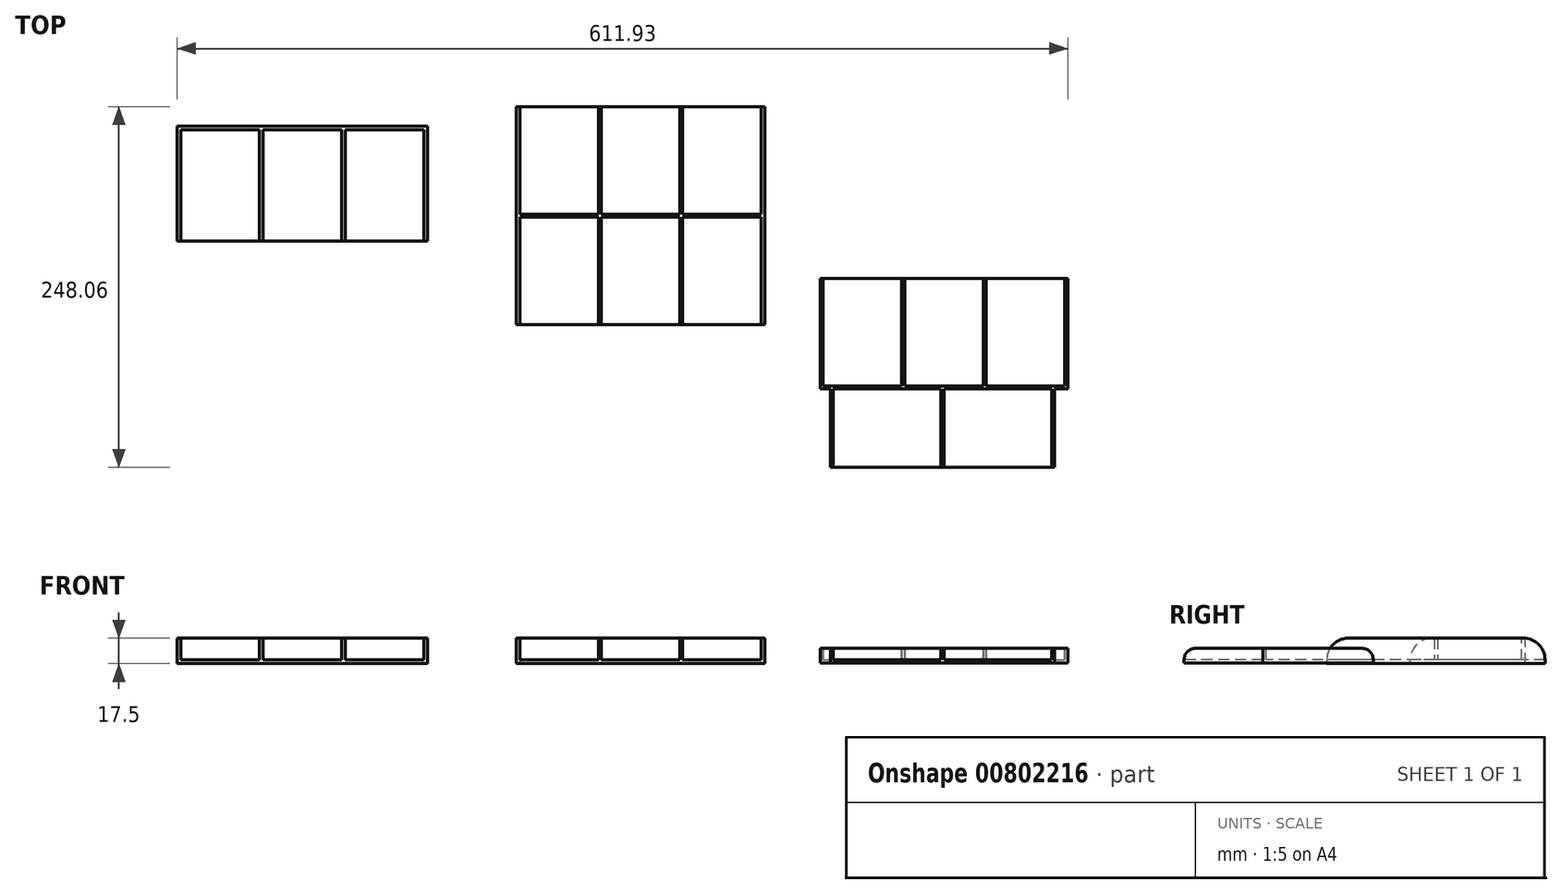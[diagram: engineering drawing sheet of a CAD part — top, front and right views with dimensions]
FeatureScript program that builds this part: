
annotation { "Feature Type Name" : "Feature", "Feature Type Description" : "" }
export const myFeature = defineFeature(function(context is Context, id is Id, definition is map)
    precondition{}
    {
        {
            var Q0;
            Q0=qCreatedBy(makeId("Top.planeOp"),FACE);
            var sketch = newSketch(context, id + "F0", { "sketchPlane" : qUnion([Q0])});
            skLineSegment(sketch, "E0.bottom", {"start": v(-93.78, 44.89) * mm, "end": v(-39.78, 44.89) * mm});
            skLineSegment(sketch, "E0.top", {"start": v(-93.78, -29.11) * mm, "end": v(-39.78, -29.11) * mm});
            skLineSegment(sketch, "E0.left", {"start": v(-93.78, 44.89) * mm, "end": v(-93.78, -29.11) * mm});
            skLineSegment(sketch, "E0.right", {"start": v(-39.78, 44.89) * mm, "end": v(-39.78, -29.11) * mm});
            skLineSegment(sketch, "E1.1.0.0", {"start": v(16.72, 44.89) * mm, "end": v(16.72, -29.11) * mm});
            skLineSegment(sketch, "E1.1.0.1", {"start": v(-37.28, -29.11) * mm, "end": v(16.72, -29.11) * mm});
            skLineSegment(sketch, "E1.1.0.2", {"start": v(-37.28, 44.89) * mm, "end": v(-37.28, -29.11) * mm});
            skLineSegment(sketch, "E1.1.0.3", {"start": v(-37.28, 44.89) * mm, "end": v(16.72, 44.89) * mm});
            skLineSegment(sketch, "E1.2.0.0", {"start": v(73.22, 44.89) * mm, "end": v(73.22, -29.11) * mm});
            skLineSegment(sketch, "E1.2.0.1", {"start": v(19.22, -29.11) * mm, "end": v(73.22, -29.11) * mm});
            skLineSegment(sketch, "E1.2.0.2", {"start": v(19.22, 44.89) * mm, "end": v(19.22, -29.11) * mm});
            skLineSegment(sketch, "E1.2.0.3", {"start": v(19.22, 44.89) * mm, "end": v(73.22, 44.89) * mm});
            skLineSegment(sketch, "E1.direction1", {"start": v(-39.78, -29.11) * mm, "end": v(16.72, -29.11) * mm, "construction": true});
            skLineSegment(sketch, "E2", {"start": v(-96.28, 47.39) * mm, "end": v(-96.28, -31.61) * mm});
            skLineSegment(sketch, "E3", {"start": v(-96.28, -31.61) * mm, "end": v(75.72, -31.61) * mm});
            skLineSegment(sketch, "E4", {"start": v(75.72, -31.61) * mm, "end": v(75.72, 47.39) * mm});
            skLineSegment(sketch, "E5", {"start": v(75.72, 47.39) * mm, "end": v(-96.28, 47.39) * mm});
            skSolve(sketch);
        }
        {
            var Q0;
            Q0=makeQuery(id+"F0.imprint","IMPRINT",FACE,{"disambiguationData":[TD([[makeQuery(id+"F0.imprint","IMPRINT",EDGE,{"derivedFrom":sQuery(id+"F0.wireOp",EDGE,"E0.bottom")}),1.0]])]});
            extrude(context, id + "F1", {"entities" : qUnion([Q0]), "depth" : 15 * mm, "offsetDistance" : 25 * mm});
        }
        {
            var Q0;
            Q0=makeQuery(id+"F1.opExtrude","CAP_FACE",FACE,{"disambiguationData":[OSD([sQuery(id+"F0.wireOp",EDGE,"E0.bottom"),sQuery(id+"F0.wireOp",EDGE,"E0.top"),sQuery(id+"F0.wireOp",EDGE,"E0.left"),sQuery(id+"F0.wireOp",EDGE,"E0.right"),sQuery(id+"F0.wireOp",EDGE,"E1.1.0.0"),sQuery(id+"F0.wireOp",EDGE,"E1.1.0.1"),sQuery(id+"F0.wireOp",EDGE,"E1.1.0.2"),sQuery(id+"F0.wireOp",EDGE,"E1.1.0.3"),sQuery(id+"F0.wireOp",EDGE,"E1.2.0.0"),sQuery(id+"F0.wireOp",EDGE,"E1.2.0.1"),sQuery(id+"F0.wireOp",EDGE,"E1.2.0.2"),sQuery(id+"F0.wireOp",EDGE,"E1.2.0.3"),sQuery(id+"F0.wireOp",EDGE,"E1.3.0.0"),sQuery(id+"F0.wireOp",EDGE,"E1.3.0.1"),sQuery(id+"F0.wireOp",EDGE,"E1.3.0.2"),sQuery(id+"F0.wireOp",EDGE,"E1.3.0.3"),sQuery(id+"F0.wireOp",EDGE,"E1.4.0.0"),sQuery(id+"F0.wireOp",EDGE,"E1.4.0.1"),sQuery(id+"F0.wireOp",EDGE,"E1.4.0.2"),sQuery(id+"F0.wireOp",EDGE,"E1.4.0.3"),sQuery(id+"F0.wireOp",EDGE,"E1.5.0.0"),sQuery(id+"F0.wireOp",EDGE,"E1.5.0.1"),sQuery(id+"F0.wireOp",EDGE,"E1.5.0.2"),sQuery(id+"F0.wireOp",EDGE,"E1.5.0.3"),sQuery(id+"F0.wireOp",EDGE,"E1.6.0.0"),sQuery(id+"F0.wireOp",EDGE,"E1.6.0.1"),sQuery(id+"F0.wireOp",EDGE,"E1.6.0.2"),sQuery(id+"F0.wireOp",EDGE,"E1.6.0.3"),sQuery(id+"F0.wireOp",EDGE,"E1.7.0.0"),sQuery(id+"F0.wireOp",EDGE,"E1.7.0.1"),sQuery(id+"F0.wireOp",EDGE,"E1.7.0.2"),sQuery(id+"F0.wireOp",EDGE,"E1.7.0.3"),sQuery(id+"F0.wireOp",EDGE,"E2"),sQuery(id+"F0.wireOp",EDGE,"E3"),sQuery(id+"F0.wireOp",EDGE,"E4"),sQuery(id+"F0.wireOp",EDGE,"E5")])],"isStart":false});
            var sketch = newSketch(context, id + "F2", { "sketchPlane" : qUnion([Q0])});
            skSolve(sketch);
        }
        {
            var Q0;
            Q0=makeQuery(id+"F2.imprint","IMPRINT",FACE,{"disambiguationData":[TD([[makeQuery(id+"F2.imprint","IMPRINT",EDGE,{"derivedFrom":makeQuery(id+"F1.opExtrude","CAP_EDGE",EDGE,{"disambiguationData":[OSD([sQuery(id+"F0.wireOp",EDGE,"E0.bottom")])],"isStart":false})}),1.0]])]});
            var Q1;
            Q1=makeQuery(id+"F2.imprint","IMPRINT",FACE,{"disambiguationData":[TD([[makeQuery(id+"F2.imprint","IMPRINT",EDGE,{"derivedFrom":makeQuery(id+"F1.opExtrude","CAP_EDGE",EDGE,{"disambiguationData":[OSD([sQuery(id+"F0.wireOp",EDGE,"E0.bottom")])],"isStart":false})}),-1.0]])]});
            var Q2;
            Q2=makeQuery(id+"F2.imprint","IMPRINT",FACE,{"disambiguationData":[TD([[makeQuery(id+"F2.imprint","IMPRINT",EDGE,{"derivedFrom":makeQuery(id+"F1.opExtrude","CAP_EDGE",EDGE,{"disambiguationData":[OSD([sQuery(id+"F0.wireOp",EDGE,"E1.1.0.0")])],"isStart":false})}),-1.0]])]});
            var Q3;
            Q3=makeQuery(id+"F2.imprint","IMPRINT",FACE,{"disambiguationData":[TD([[makeQuery(id+"F2.imprint","IMPRINT",EDGE,{"derivedFrom":makeQuery(id+"F1.opExtrude","CAP_EDGE",EDGE,{"disambiguationData":[OSD([sQuery(id+"F0.wireOp",EDGE,"E1.2.0.0")])],"isStart":false})}),-1.0]])]});
            var Q4;
            Q4=makeQuery(id+"F2.imprint","IMPRINT",FACE,{"disambiguationData":[TD([[makeQuery(id+"F2.imprint","IMPRINT",EDGE,{"derivedFrom":makeQuery(id+"F1.opExtrude","CAP_EDGE",EDGE,{"disambiguationData":[OSD([sQuery(id+"F0.wireOp",EDGE,"E1.3.0.0")])],"isStart":false})}),-1.0]])]});
            var Q5;
            Q5=makeQuery(id+"F2.imprint","IMPRINT",FACE,{"disambiguationData":[TD([[makeQuery(id+"F2.imprint","IMPRINT",EDGE,{"derivedFrom":makeQuery(id+"F1.opExtrude","CAP_EDGE",EDGE,{"disambiguationData":[OSD([sQuery(id+"F0.wireOp",EDGE,"E1.4.0.0")])],"isStart":false})}),-1.0]])]});
            var Q6;
            Q6=makeQuery(id+"F2.imprint","IMPRINT",FACE,{"disambiguationData":[TD([[makeQuery(id+"F2.imprint","IMPRINT",EDGE,{"derivedFrom":makeQuery(id+"F1.opExtrude","CAP_EDGE",EDGE,{"disambiguationData":[OSD([sQuery(id+"F0.wireOp",EDGE,"E1.5.0.0")])],"isStart":false})}),-1.0]])]});
            var Q7;
            Q7=makeQuery(id+"F2.imprint","IMPRINT",FACE,{"disambiguationData":[TD([[makeQuery(id+"F2.imprint","IMPRINT",EDGE,{"derivedFrom":makeQuery(id+"F1.opExtrude","CAP_EDGE",EDGE,{"disambiguationData":[OSD([sQuery(id+"F0.wireOp",EDGE,"E1.6.0.0")])],"isStart":false})}),-1.0]])]});
            var Q8;
            Q8=makeQuery(id+"F2.imprint","IMPRINT",FACE,{"disambiguationData":[TD([[makeQuery(id+"F2.imprint","IMPRINT",EDGE,{"derivedFrom":makeQuery(id+"F1.opExtrude","CAP_EDGE",EDGE,{"disambiguationData":[OSD([sQuery(id+"F0.wireOp",EDGE,"E1.7.0.0")])],"isStart":false})}),-1.0]])]});
            extrude(context, id + "F3", {"entities" : qUnion([Q0, Q1, Q2, Q3, Q4, Q5, Q6, Q7, Q8]), "operationType" : NewBodyOperationType.ADD, "depth" : 2.5 * mm, "offsetDistance" : 25 * mm});
        }
        {
            var Q0;
            Q0=makeQuery(id+"F1.opExtrude","SWEPT_FACE",FACE,{"disambiguationData":[OSD([sQuery(id+"F0.wireOp",EDGE,"E0.top")])]});
            var Q1;
            Q1=makeQuery(id+"F1.opExtrude","SWEPT_FACE",FACE,{"disambiguationData":[OSD([sQuery(id+"F0.wireOp",EDGE,"E1.1.0.1")])]});
            var Q2;
            Q2=makeQuery(id+"F1.opExtrude","SWEPT_FACE",FACE,{"disambiguationData":[OSD([sQuery(id+"F0.wireOp",EDGE,"E1.2.0.1")])]});
            var Q3;
            Q3=makeQuery(id+"F1.opExtrude","SWEPT_FACE",FACE,{"disambiguationData":[OSD([sQuery(id+"F0.wireOp",EDGE,"E1.3.0.1")])]});
            var Q4;
            Q4=makeQuery(id+"F1.opExtrude","SWEPT_FACE",FACE,{"disambiguationData":[OSD([sQuery(id+"F0.wireOp",EDGE,"E1.4.0.1")])]});
            var Q5;
            Q5=makeQuery(id+"F1.opExtrude","SWEPT_FACE",FACE,{"disambiguationData":[OSD([sQuery(id+"F0.wireOp",EDGE,"E1.5.0.1")])]});
            var Q6;
            Q6=makeQuery(id+"F1.opExtrude","SWEPT_FACE",FACE,{"disambiguationData":[OSD([sQuery(id+"F0.wireOp",EDGE,"E1.6.0.1")])]});
            var Q7;
            Q7=makeQuery(id+"F1.opExtrude","SWEPT_FACE",FACE,{"disambiguationData":[OSD([sQuery(id+"F0.wireOp",EDGE,"E1.7.0.1")])]});
            extrude(context, id + "F4", {"entities" : qUnion([Q0, Q1, Q2, Q3, Q4, Q5, Q6, Q7]), "operationType" : NewBodyOperationType.REMOVE, "oppositeDirection" : true, "depth" : 5 * mm, "offsetDistance" : 25 * mm});
        }
        {
            var Q0;
            {var subQ0=sQuery(id+"F0.wireOp",EDGE,"E3");var subQ1=sQuery(id+"F0.wireOp",EDGE,"E1.7.0.0");Q0=makeQuery(id+"F4.boolean.opBoolean","SPLIT",EDGE,{"disambiguationData":[TD([makeQuery(id+"F1.opExtrude","SWEPT_FACE",FACE,{"disambiguationData":[OSD([subQ1])]})])],"derivedFrom":makeQuery(id+"F1.opExtrude","CAP_EDGE",EDGE,{"disambiguationData":[OSD([subQ0])],"isStart":true})});}
            var Q1;
            {var subQ0=sQuery(id+"F0.wireOp",EDGE,"E3");var subQ4=sQuery(id+"F0.wireOp",EDGE,"E1.6.0.0");Q1=makeQuery(id+"F4.boolean.opBoolean","SPLIT",EDGE,{"disambiguationData":[TD([makeQuery(id+"F1.opExtrude","SWEPT_FACE",FACE,{"disambiguationData":[OSD([subQ4])]})])],"derivedFrom":makeQuery(id+"F1.opExtrude","CAP_EDGE",EDGE,{"disambiguationData":[OSD([subQ0])],"isStart":true})});}
            var Q2;
            {var subQ0=sQuery(id+"F0.wireOp",EDGE,"E3");var subQ2=sQuery(id+"F0.wireOp",EDGE,"E1.5.0.0");Q2=makeQuery(id+"F4.boolean.opBoolean","SPLIT",EDGE,{"disambiguationData":[TD([makeQuery(id+"F1.opExtrude","SWEPT_FACE",FACE,{"disambiguationData":[OSD([subQ2])]})])],"derivedFrom":makeQuery(id+"F1.opExtrude","CAP_EDGE",EDGE,{"disambiguationData":[OSD([subQ0])],"isStart":true})});}
            var Q3;
            {var subQ0=sQuery(id+"F0.wireOp",EDGE,"E3");var subQ2=sQuery(id+"F0.wireOp",EDGE,"E1.4.0.0");Q3=makeQuery(id+"F4.boolean.opBoolean","SPLIT",EDGE,{"disambiguationData":[TD([makeQuery(id+"F1.opExtrude","SWEPT_FACE",FACE,{"disambiguationData":[OSD([subQ2])]})])],"derivedFrom":makeQuery(id+"F1.opExtrude","CAP_EDGE",EDGE,{"disambiguationData":[OSD([subQ0])],"isStart":true})});}
            var Q4;
            {var subQ0=sQuery(id+"F0.wireOp",EDGE,"E3");var subQ2=sQuery(id+"F0.wireOp",EDGE,"E1.3.0.0");Q4=makeQuery(id+"F4.boolean.opBoolean","SPLIT",EDGE,{"disambiguationData":[TD([makeQuery(id+"F1.opExtrude","SWEPT_FACE",FACE,{"disambiguationData":[OSD([subQ2])]})])],"derivedFrom":makeQuery(id+"F1.opExtrude","CAP_EDGE",EDGE,{"disambiguationData":[OSD([subQ0])],"isStart":true})});}
            var Q5;
            {var subQ0=sQuery(id+"F0.wireOp",EDGE,"E3");var subQ2=sQuery(id+"F0.wireOp",EDGE,"E1.2.0.0");Q5=makeQuery(id+"F4.boolean.opBoolean","SPLIT",EDGE,{"disambiguationData":[TD([makeQuery(id+"F1.opExtrude","SWEPT_FACE",FACE,{"disambiguationData":[OSD([subQ2])]})])],"derivedFrom":makeQuery(id+"F1.opExtrude","CAP_EDGE",EDGE,{"disambiguationData":[OSD([subQ0])],"isStart":true})});}
            var Q6;
            {var subQ0=sQuery(id+"F0.wireOp",EDGE,"E3");var subQ4=sQuery(id+"F0.wireOp",EDGE,"E1.1.0.0");Q6=makeQuery(id+"F4.boolean.opBoolean","SPLIT",EDGE,{"disambiguationData":[TD([makeQuery(id+"F1.opExtrude","SWEPT_FACE",FACE,{"disambiguationData":[OSD([subQ4])]})])],"derivedFrom":makeQuery(id+"F1.opExtrude","CAP_EDGE",EDGE,{"disambiguationData":[OSD([subQ0])],"isStart":true})});}
            var Q7;
            {var subQ1=sQuery(id+"F0.wireOp",EDGE,"E3");var subQ2=sQuery(id+"F0.wireOp",EDGE,"E0.right");Q7=makeQuery(id+"F4.boolean.opBoolean","SPLIT",EDGE,{"disambiguationData":[TD([makeQuery(id+"F1.opExtrude","SWEPT_FACE",FACE,{"disambiguationData":[OSD([subQ2])]})])],"derivedFrom":makeQuery(id+"F1.opExtrude","CAP_EDGE",EDGE,{"disambiguationData":[OSD([subQ1])],"isStart":true})});}
            var Q8;
            {var subQ0=sQuery(id+"F0.wireOp",EDGE,"E3");var subQ2=sQuery(id+"F0.wireOp",EDGE,"E0.left");Q8=makeQuery(id+"F4.boolean.opBoolean","SPLIT",EDGE,{"disambiguationData":[TD([makeQuery(id+"F1.opExtrude","SWEPT_FACE",FACE,{"disambiguationData":[OSD([subQ2])]})])],"derivedFrom":makeQuery(id+"F1.opExtrude","CAP_EDGE",EDGE,{"disambiguationData":[OSD([subQ0])],"isStart":true})});}
            fillet(context, id + "F5", {"entities" : qUnion([Q0, Q1, Q2, Q3, Q4, Q5, Q6, Q7, Q8]), "radius" : 15 * mm, "tangentPropagation" : true, "allowEdgeOverflow" : false});
        }
        {
            var Q0;
            {var subQ0=sQuery(id+"F0.wireOp",EDGE,"E0.top");Q0=makeQuery(id+"F4.boolean.opBoolean","MERGE",FACE,{"derivedFrom":[makeQuery(id+"F3.boolean.opBoolean","SPLIT",FACE,{"disambiguationData":[TD([makeQuery(id+"F1.opExtrude","SWEPT_FACE",FACE,{"disambiguationData":[OSD([sQuery(id+"F0.wireOp",EDGE,"E0.bottom")])]})])],"derivedFrom":makeQuery(id+"F3.opExtrude","CAP_FACE",FACE,{"disambiguationData":[OSD([sQuery(id+"F0.wireOp",EDGE,"E2"),sQuery(id+"F0.wireOp",EDGE,"E3"),sQuery(id+"F0.wireOp",EDGE,"E4"),sQuery(id+"F0.wireOp",EDGE,"E5")])],"isStart":true})}),makeQuery(id+"F4.opExtrude","SWEPT_FACE",FACE,{"disambiguationData":[OSD([subQ0]),TDD([makeQuery(id+"F1.opExtrude","CAP_EDGE",EDGE,{"disambiguationData":[OSD([subQ0])],"isStart":false})])]})]});}
            var sketch = newSketch(context, id + "F6", { "sketchPlane" : qUnion([Q0])});
            skLineSegment(sketch, "E6.bottom", {"start": v(-159.66, -60.94) * mm, "end": v(-213.66, -60.94) * mm});
            skLineSegment(sketch, "E6.top", {"start": v(-159.66, 13.06) * mm, "end": v(-213.66, 13.06) * mm});
            skLineSegment(sketch, "E6.left", {"start": v(-159.66, -60.94) * mm, "end": v(-159.66, 13.06) * mm});
            skLineSegment(sketch, "E6.right", {"start": v(-213.66, -60.94) * mm, "end": v(-213.66, 13.06) * mm});
            skLineSegment(sketch, "E7.0.1.0", {"start": v(-159.66, 15.06) * mm, "end": v(-159.66, 89.06) * mm});
            skLineSegment(sketch, "E7.0.1.1", {"start": v(-159.66, 89.06) * mm, "end": v(-213.66, 89.06) * mm});
            skLineSegment(sketch, "E7.0.1.2", {"start": v(-213.66, 15.06) * mm, "end": v(-213.66, 89.06) * mm});
            skLineSegment(sketch, "E7.0.1.3", {"start": v(-159.66, 15.06) * mm, "end": v(-213.66, 15.06) * mm});
            skLineSegment(sketch, "E7.1.0.0", {"start": v(-215.66, -60.94) * mm, "end": v(-215.66, 13.06) * mm});
            skLineSegment(sketch, "E7.1.0.1", {"start": v(-215.66, 13.06) * mm, "end": v(-269.66, 13.06) * mm});
            skLineSegment(sketch, "E7.1.0.2", {"start": v(-269.66, -60.94) * mm, "end": v(-269.66, 13.06) * mm});
            skLineSegment(sketch, "E7.1.0.3", {"start": v(-215.66, -60.94) * mm, "end": v(-269.66, -60.94) * mm});
            skLineSegment(sketch, "E7.1.1.0", {"start": v(-215.66, 15.06) * mm, "end": v(-215.66, 89.06) * mm});
            skLineSegment(sketch, "E7.1.1.1", {"start": v(-215.66, 89.06) * mm, "end": v(-269.66, 89.06) * mm});
            skLineSegment(sketch, "E7.1.1.2", {"start": v(-269.66, 15.06) * mm, "end": v(-269.66, 89.06) * mm});
            skLineSegment(sketch, "E7.1.1.3", {"start": v(-215.66, 15.06) * mm, "end": v(-269.66, 15.06) * mm});
            skLineSegment(sketch, "E7.2.0.0", {"start": v(-271.66, -60.94) * mm, "end": v(-271.66, 13.06) * mm});
            skLineSegment(sketch, "E7.2.0.1", {"start": v(-271.66, 13.06) * mm, "end": v(-325.66, 13.06) * mm});
            skLineSegment(sketch, "E7.2.0.2", {"start": v(-325.66, -60.94) * mm, "end": v(-325.66, 13.06) * mm});
            skLineSegment(sketch, "E7.2.0.3", {"start": v(-271.66, -60.94) * mm, "end": v(-325.66, -60.94) * mm});
            skLineSegment(sketch, "E7.2.1.0", {"start": v(-271.66, 15.06) * mm, "end": v(-271.66, 89.06) * mm});
            skLineSegment(sketch, "E7.2.1.1", {"start": v(-271.66, 89.06) * mm, "end": v(-325.66, 89.06) * mm});
            skLineSegment(sketch, "E7.2.1.2", {"start": v(-325.66, 15.06) * mm, "end": v(-325.66, 89.06) * mm});
            skLineSegment(sketch, "E7.2.1.3", {"start": v(-271.66, 15.06) * mm, "end": v(-325.66, 15.06) * mm});
            skLineSegment(sketch, "E7.direction1", {"start": v(-213.66, -60.94) * mm, "end": v(-269.66, -60.94) * mm, "construction": true});
            skLineSegment(sketch, "E7.direction2", {"start": v(-213.66, -60.94) * mm, "end": v(-213.66, 15.06) * mm, "construction": true});
            skLineSegment(sketch, "E8", {"start": v(-325.66, -60.94) * mm, "end": v(-328.16, -60.94) * mm});
            skLineSegment(sketch, "E9", {"start": v(-328.16, -60.94) * mm, "end": v(-328.16, 89.06) * mm});
            skLineSegment(sketch, "E10", {"start": v(-328.16, 89.06) * mm, "end": v(-325.66, 89.06) * mm});
            skLineSegment(sketch, "E11", {"start": v(-159.66, 89.06) * mm, "end": v(-157.16, 89.06) * mm});
            skLineSegment(sketch, "E12", {"start": v(-157.16, 89.06) * mm, "end": v(-157.16, -60.83) * mm});
            skLineSegment(sketch, "E13", {"start": v(-157.16, -60.83) * mm, "end": v(-159.66, -60.94) * mm});
            skLineSegment(sketch, "E14", {"start": v(-213.66, -60.94) * mm, "end": v(-215.66, -60.94) * mm});
            skLineSegment(sketch, "E15", {"start": v(-269.66, -60.94) * mm, "end": v(-271.66, -60.94) * mm});
            skLineSegment(sketch, "E16", {"start": v(-271.66, 89.06) * mm, "end": v(-269.66, 89.06) * mm});
            skLineSegment(sketch, "E17", {"start": v(-215.66, 89.06) * mm, "end": v(-213.66, 89.06) * mm});
            skSolve(sketch);
        }
        {
            var Q0;
            Q0=makeQuery(id+"F6.imprint","IMPRINT",FACE,{"disambiguationData":[TD([[makeQuery(id+"F6.imprint","IMPRINT",EDGE,{"derivedFrom":sQuery(id+"F6.wireOp",EDGE,"E6.top")}),-1.0]])]});
            extrude(context, id + "F7", {"entities" : qUnion([Q0]), "depth" : 15 * mm, "offsetDistance" : 25 * mm});
        }
        {
            var Q0;
            Q0=makeQuery(id+"F6.imprint","IMPRINT",FACE,{"disambiguationData":[TD([[makeQuery(id+"F6.imprint","IMPRINT",EDGE,{"derivedFrom":sQuery(id+"F6.wireOp",EDGE,"E7.0.1.0")}),1.0]])]});
            var Q1;
            Q1=makeQuery(id+"F6.imprint","IMPRINT",FACE,{"disambiguationData":[TD([[makeQuery(id+"F6.imprint","IMPRINT",EDGE,{"derivedFrom":sQuery(id+"F6.wireOp",EDGE,"E7.1.1.0")}),1.0]])]});
            var Q2;
            Q2=makeQuery(id+"F6.imprint","IMPRINT",FACE,{"disambiguationData":[TD([[makeQuery(id+"F6.imprint","IMPRINT",EDGE,{"derivedFrom":sQuery(id+"F6.wireOp",EDGE,"E7.2.1.0")}),1.0]])]});
            var Q3;
            Q3=makeQuery(id+"F6.imprint","IMPRINT",FACE,{"disambiguationData":[TD([[makeQuery(id+"F6.imprint","IMPRINT",EDGE,{"derivedFrom":sQuery(id+"F6.wireOp",EDGE,"E7.2.0.0")}),1.0]])]});
            var Q4;
            Q4=makeQuery(id+"F6.imprint","IMPRINT",FACE,{"disambiguationData":[TD([[makeQuery(id+"F6.imprint","IMPRINT",EDGE,{"derivedFrom":sQuery(id+"F6.wireOp",EDGE,"E7.1.0.0")}),1.0]])]});
            var Q5;
            Q5=makeQuery(id+"F6.imprint","IMPRINT",FACE,{"disambiguationData":[TD([[makeQuery(id+"F6.imprint","IMPRINT",EDGE,{"derivedFrom":sQuery(id+"F6.wireOp",EDGE,"E6.bottom")}),-1.0]])]});
            var Q6;
            Q6=makeQuery(id+"F6.imprint","IMPRINT",FACE,{"disambiguationData":[TD([[makeQuery(id+"F6.imprint","IMPRINT",EDGE,{"derivedFrom":sQuery(id+"F6.wireOp",EDGE,"E6.top")}),-1.0]])]});
            extrude(context, id + "F8", {"entities" : qUnion([Q0, Q1, Q2, Q3, Q4, Q5, Q6]), "operationType" : NewBodyOperationType.ADD, "oppositeDirection" : true, "depth" : 2.5 * mm, "offsetDistance" : 25 * mm});
        }
        {
            var Q0;
            Q0=makeQuery(id+"F7.opExtrude","CAP_EDGE",EDGE,{"disambiguationData":[OSD([sQuery(id+"F6.wireOp",EDGE,"E11")])],"isStart":false});
            var Q1;
            Q1=makeQuery(id+"F7.opExtrude","CAP_EDGE",EDGE,{"disambiguationData":[OSD([sQuery(id+"F6.wireOp",EDGE,"E17")])],"isStart":false});
            var Q2;
            Q2=makeQuery(id+"F7.opExtrude","CAP_EDGE",EDGE,{"disambiguationData":[OSD([sQuery(id+"F6.wireOp",EDGE,"E13")])],"isStart":false});
            var Q3;
            Q3=makeQuery(id+"F7.opExtrude","CAP_EDGE",EDGE,{"disambiguationData":[OSD([sQuery(id+"F6.wireOp",EDGE,"E14")])],"isStart":false});
            var Q4;
            Q4=makeQuery(id+"F7.opExtrude","CAP_EDGE",EDGE,{"disambiguationData":[OSD([sQuery(id+"F6.wireOp",EDGE,"E15")])],"isStart":false});
            var Q5;
            Q5=makeQuery(id+"F7.opExtrude","CAP_EDGE",EDGE,{"disambiguationData":[OSD([sQuery(id+"F6.wireOp",EDGE,"E8")])],"isStart":false});
            var Q6;
            Q6=makeQuery(id+"F7.opExtrude","CAP_EDGE",EDGE,{"disambiguationData":[OSD([sQuery(id+"F6.wireOp",EDGE,"E10")])],"isStart":false});
            var Q7;
            Q7=makeQuery(id+"F7.opExtrude","CAP_EDGE",EDGE,{"disambiguationData":[OSD([sQuery(id+"F6.wireOp",EDGE,"E16")])],"isStart":false});
            fillet(context, id + "F9", {"entities" : qUnion([Q0, Q1, Q2, Q3, Q4, Q5, Q6, Q7]), "radius" : 15 * mm, "tangentPropagation" : true, "allowEdgeOverflow" : false});
        }
        {
            var Q0;
            {var subQ0=sQuery(id+"F6.wireOp",EDGE,"E17");var subQ1=sQuery(id+"F6.wireOp",EDGE,"E16");var subQ2=sQuery(id+"F6.wireOp",EDGE,"E11");var subQ3=sQuery(id+"F6.wireOp",EDGE,"E10");var subQ4=sQuery(id+"F6.wireOp",EDGE,"E7.2.1.1");var subQ5=sQuery(id+"F6.wireOp",EDGE,"E7.1.1.1");var subQ6=sQuery(id+"F6.wireOp",EDGE,"E7.0.1.1");Q0=makeQuery(id+"F8.boolean.opBoolean","SPLIT",FACE,{"disambiguationData":[TD([makeQuery(id+"F7.opExtrude","SWEPT_FACE",FACE,{"disambiguationData":[OSD([sQuery(id+"F6.wireOp",EDGE,"E7.2.1.0")])]})])],"derivedFrom":makeQuery(id+"F8.opExtrude","CAP_FACE",FACE,{"disambiguationData":[OSD([sQuery(id+"F6.wireOp",EDGE,"E6.bottom"),subQ6,sQuery(id+"F6.wireOp",EDGE,"E7.1.0.3"),subQ5,sQuery(id+"F6.wireOp",EDGE,"E7.2.0.3"),subQ4,sQuery(id+"F6.wireOp",EDGE,"E8"),sQuery(id+"F6.wireOp",EDGE,"E9"),subQ3,subQ2,sQuery(id+"F6.wireOp",EDGE,"E12"),sQuery(id+"F6.wireOp",EDGE,"E13"),sQuery(id+"F6.wireOp",EDGE,"E14"),sQuery(id+"F6.wireOp",EDGE,"E15"),subQ1,subQ0])],"isStart":true})});}
            var sketch = newSketch(context, id + "F10", { "sketchPlane" : qUnion([Q0])});
            skLineSegment(sketch, "E18.bottom", {"start": v(-368.2, 57.12) * mm, "end": v(-422.2, 57.12) * mm});
            skLineSegment(sketch, "E18.top", {"start": v(-368.2, 131.12) * mm, "end": v(-422.2, 131.12) * mm});
            skLineSegment(sketch, "E18.left", {"start": v(-368.2, 57.12) * mm, "end": v(-368.2, 131.12) * mm});
            skLineSegment(sketch, "E18.right", {"start": v(-422.2, 57.12) * mm, "end": v(-422.2, 131.12) * mm});
            skLineSegment(sketch, "E19.1.0.0", {"start": v(-478.2, 57.12) * mm, "end": v(-478.2, 131.12) * mm});
            skLineSegment(sketch, "E19.1.0.1", {"start": v(-424.2, 57.12) * mm, "end": v(-478.2, 57.12) * mm});
            skLineSegment(sketch, "E19.1.0.2", {"start": v(-424.2, 131.12) * mm, "end": v(-478.2, 131.12) * mm});
            skLineSegment(sketch, "E19.1.0.3", {"start": v(-424.2, 57.12) * mm, "end": v(-424.2, 131.12) * mm});
            skLineSegment(sketch, "E19.2.0.0", {"start": v(-534.2, 57.12) * mm, "end": v(-534.2, 131.12) * mm});
            skLineSegment(sketch, "E19.2.0.1", {"start": v(-480.2, 57.12) * mm, "end": v(-534.2, 57.12) * mm});
            skLineSegment(sketch, "E19.2.0.2", {"start": v(-480.2, 131.12) * mm, "end": v(-534.2, 131.12) * mm});
            skLineSegment(sketch, "E19.2.0.3", {"start": v(-480.2, 57.12) * mm, "end": v(-480.2, 131.12) * mm});
            skLineSegment(sketch, "E19.direction1", {"start": v(-422.2, 57.12) * mm, "end": v(-478.2, 57.12) * mm, "construction": true});
            skLineSegment(sketch, "E20.bottom", {"start": v(-375.2, 133.12) * mm, "end": v(-449.2, 133.12) * mm});
            skLineSegment(sketch, "E20.top", {"start": v(-375.2, 187.12) * mm, "end": v(-449.2, 187.12) * mm});
            skLineSegment(sketch, "E20.left", {"start": v(-375.2, 133.12) * mm, "end": v(-375.2, 187.12) * mm});
            skLineSegment(sketch, "E20.right", {"start": v(-449.2, 133.12) * mm, "end": v(-449.2, 187.12) * mm});
            skLineSegment(sketch, "E21", {"start": v(-450.2, 57.12) * mm, "end": v(-450.2, 207.09) * mm, "construction": true});
            skLineSegment(sketch, "E22.MirrorCS", {"start": v(-525.2, 187.12) * mm, "end": v(-451.2, 187.12) * mm});
            skLineSegment(sketch, "E23.MirrorCS", {"start": v(-525.2, 133.12) * mm, "end": v(-525.2, 187.12) * mm});
            skLineSegment(sketch, "E24.MirrorCS", {"start": v(-525.2, 133.12) * mm, "end": v(-451.2, 133.12) * mm});
            skLineSegment(sketch, "E25.MirrorCS", {"start": v(-451.2, 133.12) * mm, "end": v(-451.2, 187.12) * mm});
            skLineSegment(sketch, "E26", {"start": v(-368.2, 57.12) * mm, "end": v(-366.2, 57.12) * mm});
            skLineSegment(sketch, "E27", {"start": v(-366.2, 57.12) * mm, "end": v(-366.2, 133.24) * mm});
            skLineSegment(sketch, "E28", {"start": v(-366.2, 133.24) * mm, "end": v(-375.2, 133.12) * mm});
            skLineSegment(sketch, "E29", {"start": v(-534.2, 57.12) * mm, "end": v(-536.2, 57.12) * mm});
            skLineSegment(sketch, "E30", {"start": v(-536.2, 57.12) * mm, "end": v(-536.2, 133.12) * mm});
            skLineSegment(sketch, "E31", {"start": v(-536.2, 133.12) * mm, "end": v(-525.2, 133.12) * mm});
            skLineSegment(sketch, "E32", {"start": v(-525.2, 187.12) * mm, "end": v(-527.2, 187.12) * mm});
            skLineSegment(sketch, "E33", {"start": v(-527.2, 187.12) * mm, "end": v(-527.2, 133.12) * mm});
            skLineSegment(sketch, "E34", {"start": v(-375.2, 187.12) * mm, "end": v(-373.2, 187.12) * mm});
            skLineSegment(sketch, "E35", {"start": v(-373.2, 187.12) * mm, "end": v(-373.2, 133.15) * mm});
            skLineSegment(sketch, "E36", {"start": v(-449.2, 187.12) * mm, "end": v(-451.2, 187.12) * mm});
            skLineSegment(sketch, "E37", {"start": v(-424.2, 57.12) * mm, "end": v(-422.2, 57.12) * mm});
            skLineSegment(sketch, "E38", {"start": v(-478.2, 57.12) * mm, "end": v(-480.2, 57.12) * mm});
            skSolve(sketch);
        }
        {
            var Q0;
            Q0=makeQuery(id+"F10.imprint","IMPRINT",FACE,{"disambiguationData":[TD([[makeQuery(id+"F10.imprint","IMPRINT",EDGE,{"derivedFrom":sQuery(id+"F10.wireOp",EDGE,"E18.top")}),-1.0]])]});
            var Q1;
            {var subQ0=sQuery(id+"F10.wireOp",EDGE,"E20.left");Q1=makeQuery(id+"F10.imprint","IMPRINT",FACE,{"disambiguationData":[TD([[makeQuery(id+"F10.imprint","IMPRINT",EDGE,{"derivedFrom":subQ0}),-1.0]])]});}
            var Q2;
            {var subQ0=sQuery(id+"F10.wireOp",EDGE,"E23.MirrorCS");Q2=makeQuery(id+"F10.imprint","IMPRINT",FACE,{"disambiguationData":[TD([[makeQuery(id+"F10.imprint","IMPRINT",EDGE,{"derivedFrom":subQ0}),1.0]])]});}
            extrude(context, id + "F11", {"entities" : qUnion([Q0, Q1, Q2]), "depth" : 8 * mm, "offsetDistance" : 25 * mm});
        }
        {
            var Q0;
            {var subQ0=sQuery(id+"F10.wireOp",EDGE,"E20.left");Q0=makeQuery(id+"F10.imprint","IMPRINT",FACE,{"disambiguationData":[TD([[makeQuery(id+"F10.imprint","IMPRINT",EDGE,{"derivedFrom":subQ0}),-1.0]])]});}
            var Q1;
            Q1=makeQuery(id+"F10.imprint","IMPRINT",FACE,{"disambiguationData":[TD([[makeQuery(id+"F10.imprint","IMPRINT",EDGE,{"derivedFrom":sQuery(id+"F10.wireOp",EDGE,"E18.top")}),-1.0]])]});
            var Q2;
            Q2=makeQuery(id+"F10.imprint","IMPRINT",FACE,{"disambiguationData":[TD([[makeQuery(id+"F10.imprint","IMPRINT",EDGE,{"derivedFrom":sQuery(id+"F10.wireOp",EDGE,"E20.bottom")}),-1.0]])]});
            var Q3;
            Q3=makeQuery(id+"F10.imprint","IMPRINT",FACE,{"disambiguationData":[TD([[makeQuery(id+"F10.imprint","IMPRINT",EDGE,{"derivedFrom":sQuery(id+"F10.wireOp",EDGE,"E18.bottom")}),-1.0]])]});
            var Q4;
            Q4=makeQuery(id+"F10.imprint","IMPRINT",FACE,{"disambiguationData":[TD([[makeQuery(id+"F10.imprint","IMPRINT",EDGE,{"derivedFrom":sQuery(id+"F10.wireOp",EDGE,"E19.1.0.0")}),-1.0]])]});
            var Q5;
            Q5=makeQuery(id+"F10.imprint","IMPRINT",FACE,{"disambiguationData":[TD([[makeQuery(id+"F10.imprint","IMPRINT",EDGE,{"derivedFrom":sQuery(id+"F10.wireOp",EDGE,"E19.2.0.0")}),-1.0]])]});
            var Q6;
            {var subQ0=sQuery(id+"F10.wireOp",EDGE,"E23.MirrorCS");Q6=makeQuery(id+"F10.imprint","IMPRINT",FACE,{"disambiguationData":[TD([[makeQuery(id+"F10.imprint","IMPRINT",EDGE,{"derivedFrom":subQ0}),1.0]])]});}
            var Q7;
            Q7=makeQuery(id+"F10.imprint","IMPRINT",FACE,{"disambiguationData":[TD([[makeQuery(id+"F10.imprint","IMPRINT",EDGE,{"derivedFrom":sQuery(id+"F10.wireOp",EDGE,"E22.MirrorCS")}),-1.0]])]});
            extrude(context, id + "F12", {"entities" : qUnion([Q0, Q1, Q2, Q3, Q4, Q5, Q6, Q7]), "operationType" : NewBodyOperationType.ADD, "oppositeDirection" : true, "depth" : 2 * mm, "offsetDistance" : 25 * mm});
        }
        {
            var Q0;
            Q0=makeQuery(id+"F11.opExtrude","CAP_EDGE",EDGE,{"disambiguationData":[OSD([sQuery(id+"F10.wireOp",EDGE,"E34")])],"isStart":false});
            var Q1;
            Q1=makeQuery(id+"F11.opExtrude","CAP_EDGE",EDGE,{"disambiguationData":[OSD([sQuery(id+"F10.wireOp",EDGE,"E26")])],"isStart":false});
            var Q2;
            Q2=makeQuery(id+"F11.opExtrude","CAP_EDGE",EDGE,{"disambiguationData":[OSD([sQuery(id+"F10.wireOp",EDGE,"E37")])],"isStart":false});
            var Q3;
            Q3=makeQuery(id+"F11.opExtrude","CAP_EDGE",EDGE,{"disambiguationData":[OSD([sQuery(id+"F10.wireOp",EDGE,"E36")])],"isStart":false});
            var Q4;
            Q4=makeQuery(id+"F11.opExtrude","CAP_EDGE",EDGE,{"disambiguationData":[OSD([sQuery(id+"F10.wireOp",EDGE,"E32")])],"isStart":false});
            var Q5;
            Q5=makeQuery(id+"F11.opExtrude","CAP_EDGE",EDGE,{"disambiguationData":[OSD([sQuery(id+"F10.wireOp",EDGE,"E29")])],"isStart":false});
            var Q6;
            Q6=makeQuery(id+"F11.opExtrude","CAP_EDGE",EDGE,{"disambiguationData":[OSD([sQuery(id+"F10.wireOp",EDGE,"E38")])],"isStart":false});
            fillet(context, id + "F13", {"entities" : qUnion([Q0, Q1, Q2, Q3, Q4, Q5, Q6]), "radius" : 8 * mm, "tangentPropagation" : true, "allowEdgeOverflow" : false});
        }
        {
            var Q0;
            Q0=makeQuery(id+"F11.opExtrude","SWEPT_BODY",BODY,{"disambiguationData":[OSD([sQuery(id+"F10.wireOp",EDGE,"E18.top"),sQuery(id+"F10.wireOp",EDGE,"E18.left"),sQuery(id+"F10.wireOp",EDGE,"E18.right"),sQuery(id+"F10.wireOp",EDGE,"E19.1.0.0"),sQuery(id+"F10.wireOp",EDGE,"E19.1.0.2"),sQuery(id+"F10.wireOp",EDGE,"E19.1.0.3"),sQuery(id+"F10.wireOp",EDGE,"E19.2.0.0"),sQuery(id+"F10.wireOp",EDGE,"E19.2.0.2"),sQuery(id+"F10.wireOp",EDGE,"E19.2.0.3"),sQuery(id+"F10.wireOp",EDGE,"E20.bottom"),sQuery(id+"F10.wireOp",EDGE,"E20.left"),sQuery(id+"F10.wireOp",EDGE,"E20.right"),sQuery(id+"F10.wireOp",EDGE,"E23.MirrorCS"),sQuery(id+"F10.wireOp",EDGE,"E24.MirrorCS"),sQuery(id+"F10.wireOp",EDGE,"E25.MirrorCS"),sQuery(id+"F10.wireOp",EDGE,"E26"),sQuery(id+"F10.wireOp",EDGE,"E27"),sQuery(id+"F10.wireOp",EDGE,"E28"),sQuery(id+"F10.wireOp",EDGE,"E29"),sQuery(id+"F10.wireOp",EDGE,"E30"),sQuery(id+"F10.wireOp",EDGE,"E31"),sQuery(id+"F10.wireOp",EDGE,"E32"),sQuery(id+"F10.wireOp",EDGE,"E33"),sQuery(id+"F10.wireOp",EDGE,"E34"),sQuery(id+"F10.wireOp",EDGE,"E35"),sQuery(id+"F10.wireOp",EDGE,"E36"),sQuery(id+"F10.wireOp",EDGE,"E37"),sQuery(id+"F10.wireOp",EDGE,"E38")])]});
            var Q1;
            Q1=makeQuery(id+"F7.opExtrude","SWEPT_BODY",BODY,{"disambiguationData":[OSD([sQuery(id+"F6.wireOp",EDGE,"E6.top"),sQuery(id+"F6.wireOp",EDGE,"E6.left"),sQuery(id+"F6.wireOp",EDGE,"E6.right"),sQuery(id+"F6.wireOp",EDGE,"E7.0.1.0"),sQuery(id+"F6.wireOp",EDGE,"E7.0.1.2"),sQuery(id+"F6.wireOp",EDGE,"E7.0.1.3"),sQuery(id+"F6.wireOp",EDGE,"E7.1.0.0"),sQuery(id+"F6.wireOp",EDGE,"E7.1.0.1"),sQuery(id+"F6.wireOp",EDGE,"E7.1.0.2"),sQuery(id+"F6.wireOp",EDGE,"E7.1.1.0"),sQuery(id+"F6.wireOp",EDGE,"E7.1.1.2"),sQuery(id+"F6.wireOp",EDGE,"E7.1.1.3"),sQuery(id+"F6.wireOp",EDGE,"E7.2.0.0"),sQuery(id+"F6.wireOp",EDGE,"E7.2.0.1"),sQuery(id+"F6.wireOp",EDGE,"E7.2.0.2"),sQuery(id+"F6.wireOp",EDGE,"E7.2.1.0"),sQuery(id+"F6.wireOp",EDGE,"E7.2.1.2"),sQuery(id+"F6.wireOp",EDGE,"E7.2.1.3"),sQuery(id+"F6.wireOp",EDGE,"E8"),sQuery(id+"F6.wireOp",EDGE,"E9"),sQuery(id+"F6.wireOp",EDGE,"E10"),sQuery(id+"F6.wireOp",EDGE,"E11"),sQuery(id+"F6.wireOp",EDGE,"E12"),sQuery(id+"F6.wireOp",EDGE,"E13"),sQuery(id+"F6.wireOp",EDGE,"E14"),sQuery(id+"F6.wireOp",EDGE,"E15"),sQuery(id+"F6.wireOp",EDGE,"E16"),sQuery(id+"F6.wireOp",EDGE,"E17")])]});
            var Q2;
            Q2=makeQuery(id+"F1.opExtrude","SWEPT_BODY",BODY,{"disambiguationData":[OSD([sQuery(id+"F0.wireOp",EDGE,"E0.bottom"),sQuery(id+"F0.wireOp",EDGE,"E0.top"),sQuery(id+"F0.wireOp",EDGE,"E0.left"),sQuery(id+"F0.wireOp",EDGE,"E0.right"),sQuery(id+"F0.wireOp",EDGE,"E1.1.0.0"),sQuery(id+"F0.wireOp",EDGE,"E1.1.0.1"),sQuery(id+"F0.wireOp",EDGE,"E1.1.0.2"),sQuery(id+"F0.wireOp",EDGE,"E1.1.0.3"),sQuery(id+"F0.wireOp",EDGE,"E1.2.0.0"),sQuery(id+"F0.wireOp",EDGE,"E1.2.0.1"),sQuery(id+"F0.wireOp",EDGE,"E1.2.0.2"),sQuery(id+"F0.wireOp",EDGE,"E1.2.0.3"),sQuery(id+"F0.wireOp",EDGE,"E2"),sQuery(id+"F0.wireOp",EDGE,"E3"),sQuery(id+"F0.wireOp",EDGE,"E4"),sQuery(id+"F0.wireOp",EDGE,"E5")])]});
            var Q3;
            Q3=makeQuery(id+"F8.opExtrude","CAP_EDGE",EDGE,{"disambiguationData":[OSD([sQuery(id+"F6.wireOp",EDGE,"E9")])],"isStart":false});
            transform(context, id + "F14", {"entities" : qUnion([Q0, Q1, Q2]), "transformType" : TransformType.ROTATION, "transformAxis" : qUnion([Q3]), "angle" : 180 * degree, "makeCopy" : false});
        }
    });
